# Revit family: CRN
name_source: partatom
category: Lighting Fixtures
units: mm (PartAtom-declared; Revit-internal decimal feet)

## family parameters
Cut with Voids When Loaded = No
Host = Face
Light Source = Yes
OmniClass Number = 23.80.70.11.14.11
OmniClass Title = Downlights
Part Type = Normal
Room Calculation Point = No
Round Connector Dimension = Use Diameter
Shared = Yes

## types (1)
- CRN
    Apparent Load = 0 VA
    Application = Industrial/Warehouse/Mezzanine/Garden Center/Big Box Retail/Auditorium/Gymnasium
    Assembly Code = D5020200
    Certification = All luminaires are built to UL1598 standards, and bear appropriate
cULus labels for wet location/IP65
    Color Filter = 16777215
    Color Rendering Inde (CRI) = 80
    Controls = Occupancy & Photocell
    Default Elevation = 48 "
    Description = The CRN is an efficient wet location high bay suitable for a variety of areas including warehouses, gyms, covered outdoor areas, garden centers, and mezzanines.
    Dimming Lamp Color Temperature Shift = <None>
    Dimming Protocol = 0-10V
    Emit Shape Visible in Rendering = No
    Emit from Circle Diameter = 14.9 "
    Features = Offers lumen packages from 14,000 to 34,000 lms for proper illumination on a variety of high bay applications.
Efficacy up to 146 lms/w assures you energy savings over traditional high bay luminaires.
Modify your aesthetic and reduce glare with clear, diffuse or aluminum reflector options.
Customize light levels and illumination schedules with a programmable occupancy/photocell sensor that will dim your CRN to 10%
Wet location and IP65 ratings make the CRN an ideal choice for both general and demanding spaces.
Thermally separated electronic and LED heat sink design enables long, trouble free operation.
L70 at 54,000 hrs
DLC® (DesignLights Consortium) Premium Qualified - see www.designlights.org
    Glass = Glass -  White
    Housing Material = Paint -  White
    LED = LED - Material
    Lamp = LED
    Load Classification = Lighting
    Manufacturer = Columbia Lighting
    Model = Wer Location High Bay
    Mounting = Pendant/Yoke Mount/ Suspended
    Photometric Notes = More IES files download on Photometric Link
    Photometric Web File = CRN-40LX-EDU.ies
    Power Factor = 1
    Product Category = High Bay/Low Bay
    Tilt Angle = -90.00°
    Type Comments = Lighting Fixture
    URL = https://www.currentlighting.com
    Voltage = 120 V
    Warranty = 5-Years Warranty

## geometry (parser evidence)
native form markers: Sweep x1
no freeform markers — native parametric forms only
